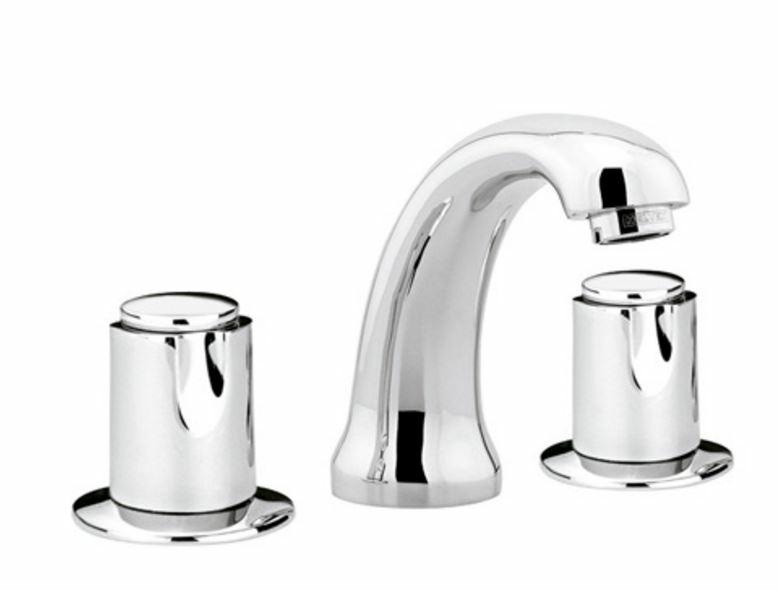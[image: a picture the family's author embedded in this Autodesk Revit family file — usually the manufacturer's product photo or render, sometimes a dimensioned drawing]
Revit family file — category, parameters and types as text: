
# Revit family: Mezcladora de Lavabo MEP-2009
name_source: partatom
category: Aparatos sanitarios
revit_build: Autodesk Revit 2016 (Build: 20150220_1215(x64)
units: mm (PartAtom-declared; Revit-internal decimal feet)

## family parameters
Compartido = Sí
Corte con vacíos al cargar = No
Cota de conector redondo = Diámetro de uso
Número OmniClass = 23.45.55.17
Punto de cálculo de habitación = Sí
Se basa en plano de trabajo = Sí
Siempre vertical = Sí
Tipo de pieza = Normal
Título OmniClass = Mixing Faucets

## types (1)
- MEP-2009
    Brass Chromed = Brass
    Comentarios de tipo = Lavatory Faucet Assemblies
    Descripción = Faucet Cibeles 8" To 12" With Push Drain
    Elevación por Defecto = 1"
    Elevación por defecto = 1"
    Fabricante = HELVEX
    Features = Valvex I Compression Left
    Imagen de tipo = MEP-2009.JPG
    Inlet Threads = ½" - 14 NPSM
    Installation Adjustment = 8", 10" Or 12"
    Instructive = http://www.helvex.com.mx
    Max. Working Pressure = 85.3 psi
    Min. Working Pressure = 3.6 psi
    Modelo = MEP-2009
    Total Height = 5"
    Total Length = 12"
    Total Width = 4"
    URL = http://www.helvex.com.mx

## geometry (parser evidence)
native form markers: Sweep x3
no freeform markers — native parametric forms only
